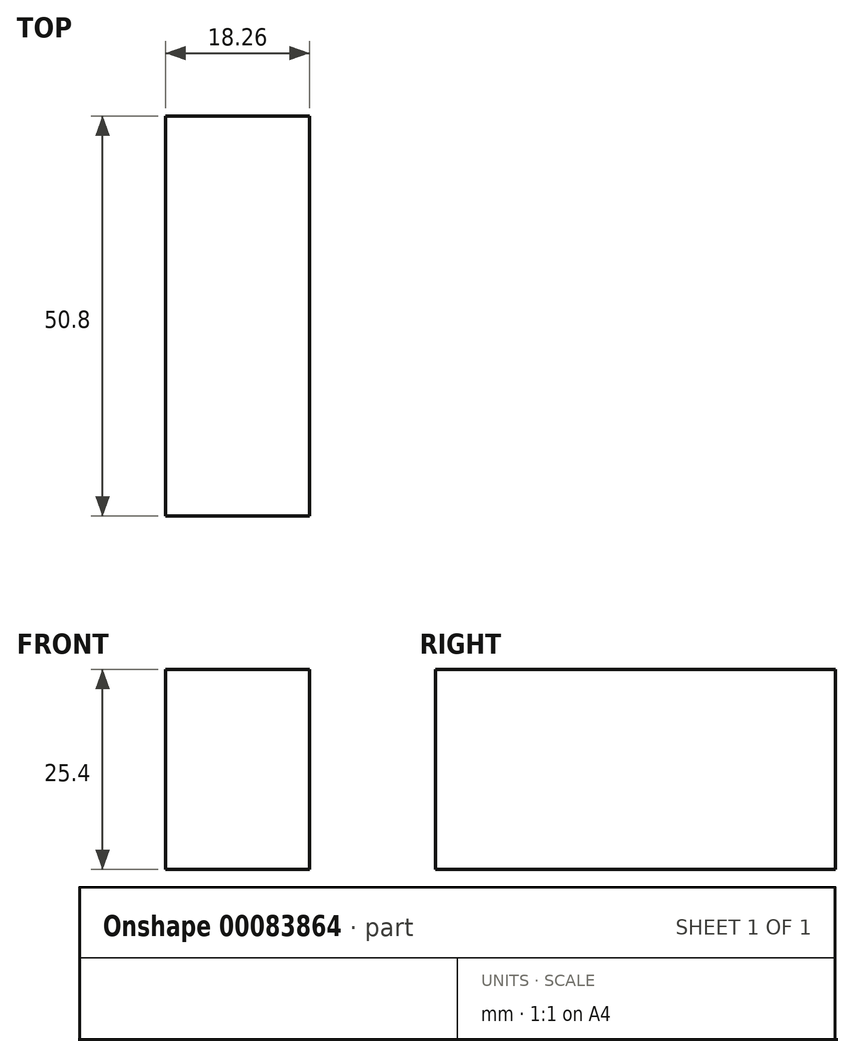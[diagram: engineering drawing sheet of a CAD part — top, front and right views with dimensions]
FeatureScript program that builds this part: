
annotation { "Feature Type Name" : "Feature", "Feature Type Description" : "" }
export const myFeature = defineFeature(function(context is Context, id is Id, definition is map)
    precondition{}
    {
        {
            var Q0;
            Q0=qCreatedBy(makeId("Top.planeOp"),FACE);
            var sketch = newSketch(context, id + "F0", { "sketchPlane" : qUnion([Q0])});
            skLineSegment(sketch, "E0.bottom", {"start": v(0, 0) * mm, "end": v(18.26, 0) * mm});
            skLineSegment(sketch, "E0.top", {"start": v(0, 50.8) * mm, "end": v(18.26, 50.8) * mm});
            skLineSegment(sketch, "E0.left", {"start": v(0, 0) * mm, "end": v(0, 50.8) * mm});
            skLineSegment(sketch, "E0.right", {"start": v(18.26, 0) * mm, "end": v(18.26, 50.8) * mm});
            skSolve(sketch);
        }
        {
            var Q0;
            Q0=makeQuery(id+"F0.imprint","IMPRINT",FACE,{"disambiguationData":[TD([[makeQuery(id+"F0.imprint","IMPRINT",EDGE,{"derivedFrom":sQuery(id+"F0.wireOp",EDGE,"E0.bottom")}),1.0]])]});
            extrude(context, id + "F1", {"entities" : qUnion([Q0]), "depth" : 25.4 * mm});
        }
    });
